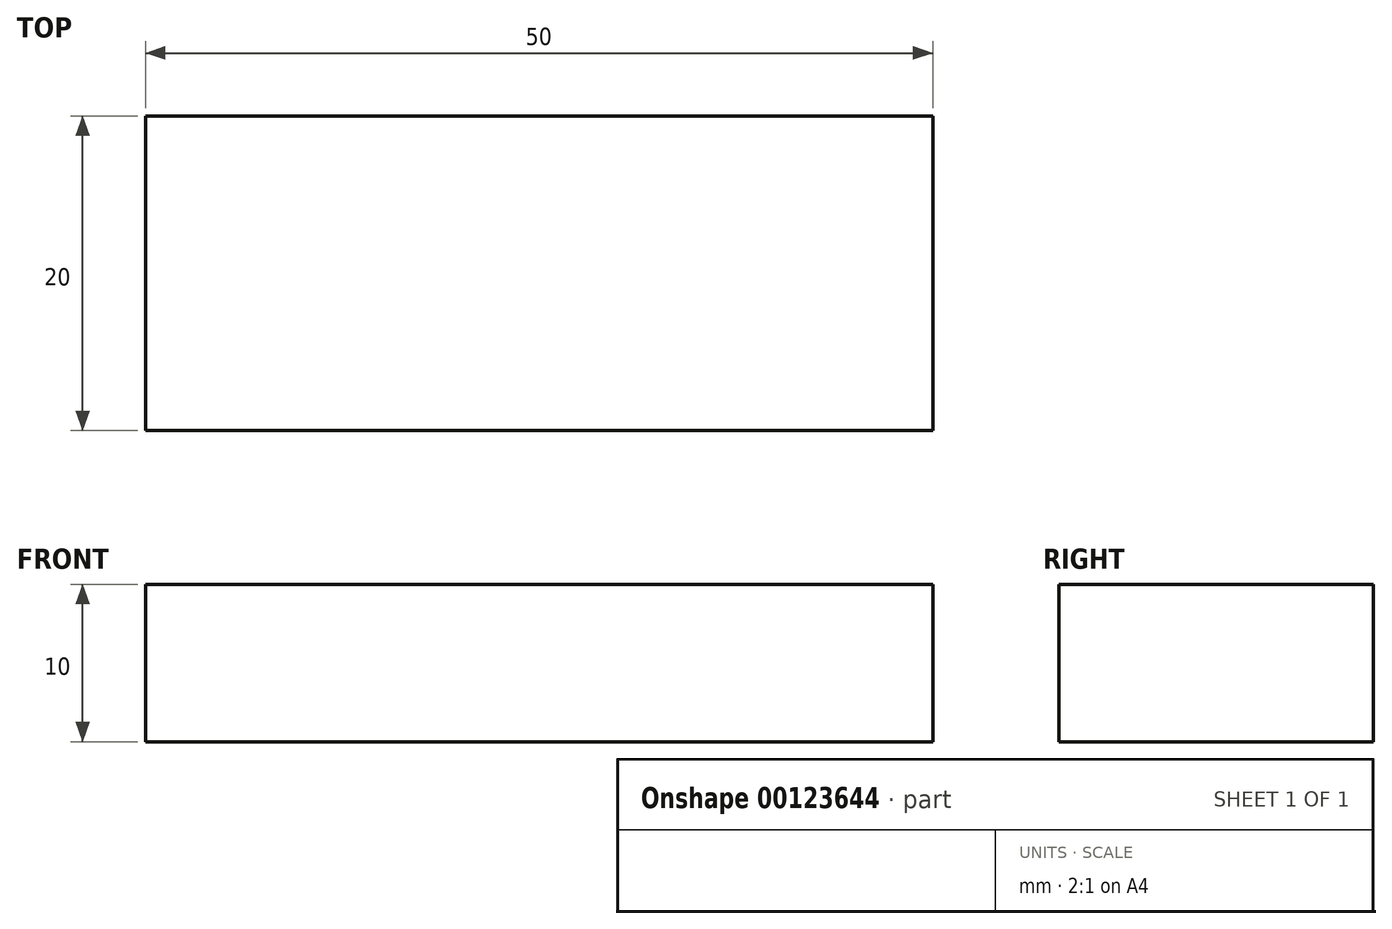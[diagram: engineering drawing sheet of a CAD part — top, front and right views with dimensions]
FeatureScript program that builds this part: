
annotation { "Feature Type Name" : "Feature", "Feature Type Description" : "" }
export const myFeature = defineFeature(function(context is Context, id is Id, definition is map)
    precondition{}
    {
        {
            var Q0;
            Q0=qCreatedBy(makeId("Top.planeOp"),FACE);
            var sketch = newSketch(context, id + "F0", { "sketchPlane" : qUnion([Q0])});
            skLineSegment(sketch, "E0.bottom", {"start": v(-19.7, 10.95) * mm, "end": v(30.3, 10.95) * mm});
            skLineSegment(sketch, "E0.top", {"start": v(-19.7, -9.05) * mm, "end": v(30.3, -9.05) * mm});
            skLineSegment(sketch, "E0.left", {"start": v(-19.7, 10.95) * mm, "end": v(-19.7, -9.05) * mm});
            skLineSegment(sketch, "E0.right", {"start": v(30.3, 10.95) * mm, "end": v(30.3, -9.05) * mm});
            skSolve(sketch);
        }
        {
            var Q0;
            Q0 = qSketchRegion(id + "F0", true);
            extrude(context, id + "F1", {"entities" : qUnion([Q0]), "depth" : 10 * mm});
        }
    });
